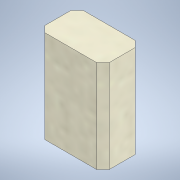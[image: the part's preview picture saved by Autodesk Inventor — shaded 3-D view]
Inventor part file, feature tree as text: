
AUTODESK INVENTOR PART (.ipt)
format: ipt  version: 2021 (Build 250183000, 183)  size: 114,688 bytes
history: native  units: mm
features: extrude x1, sketch x1
ambient origin geometry x8: Origin, YZ Plane, XZ Plane, XY Plane, X Axis, Y Axis, Z Axis, Center Point
bodies: Solid1 (feature_tree)
feature tree (2):
  extrude  "Extrusion1"  Depth=12.5mm
  sketch  "Sketch1"  dims[d0=20.9mm d1=12.5mm d2=2.0mm d3=2.0mm d10=30.1mm d11=0.0mm]
